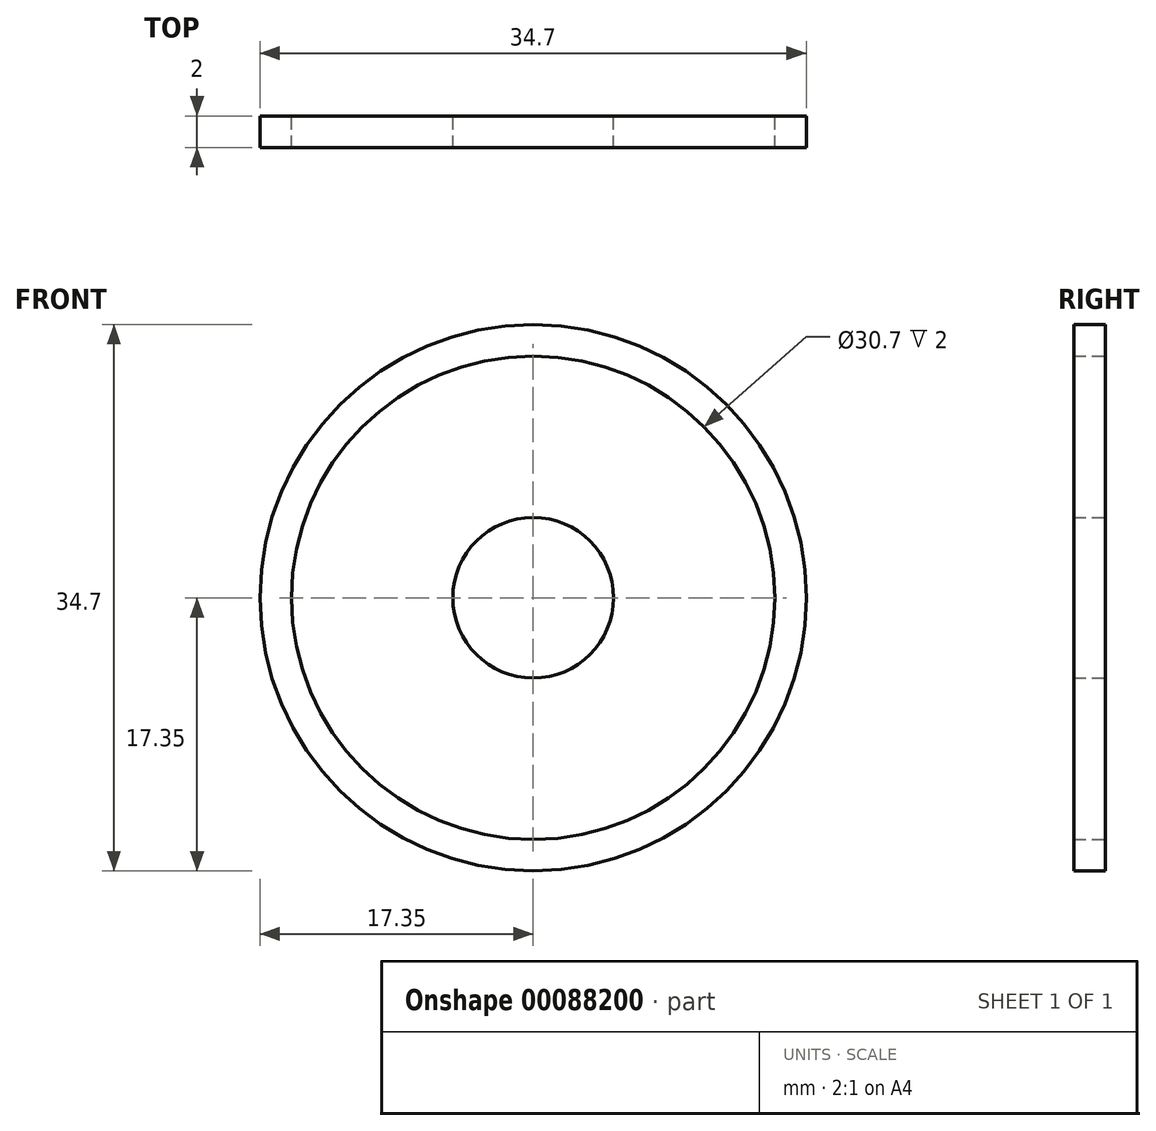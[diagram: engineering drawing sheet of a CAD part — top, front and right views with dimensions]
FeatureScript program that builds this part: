
annotation { "Feature Type Name" : "Feature", "Feature Type Description" : "" }
export const myFeature = defineFeature(function(context is Context, id is Id, definition is map)
    precondition{}
    {
        {
            var Q0;
            Q0=qCreatedBy(makeId("Front.planeOp"),FACE);
            var sketch = newSketch(context, id + "F0", { "sketchPlane" : qUnion([Q0])});
            skCircle(sketch, "E0", {"center": v(0, 0) * mm, "radius": 15.35 * mm});
            skCircle(sketch, "E1", {"center": v(0, 0) * mm, "radius": 5.1 * mm});
            skCircle(sketch, "E2.0", {"center": v(0, 0) * mm, "radius": 17.35 * mm});
            skCircle(sketch, "E3.0", {"center": v(0, 0) * mm, "radius": 3 * mm});
            skLineSegment(sketch, "E4", {"start": v(0, 3) * mm, "end": v(0, 3) * mm});
            skLineSegment(sketch, "E5", {"start": v(0, 3) * mm, "end": v(0, 5.1) * mm});
            skLineSegment(sketch, "E6", {"start": v(0, 5.1) * mm, "end": v(0, 1.6) * mm});
            skSolve(sketch);
        }
        {
            var Q0;
            Q0=makeQuery(id+"F0.imprint","IMPRINT",FACE,{"disambiguationData":[TD([[makeQuery(id+"F0.imprint","IMPRINT",EDGE,{"derivedFrom":sQuery(id+"F0.wireOp",EDGE,"E3.0")}),1.0]])]});
            var Q1;
            Q1=makeQuery(id+"F0.imprint","IMPRINT",FACE,{"disambiguationData":[TD([[makeQuery(id+"F0.imprint","IMPRINT",EDGE,{"derivedFrom":sQuery(id+"F0.wireOp",EDGE,"E1")}),1.0]])]});
            var Q2;
            Q2=makeQuery(id+"F0.imprint","IMPRINT",FACE,{"disambiguationData":[TD([[makeQuery(id+"F0.imprint","IMPRINT",EDGE,{"derivedFrom":sQuery(id+"F0.wireOp",EDGE,"E0")}),-1.0]])]});
            extrude(context, id + "F1", {"entities" : qUnion([Q0, Q1, Q2]), "depth" : 2 * mm});
        }
    });
